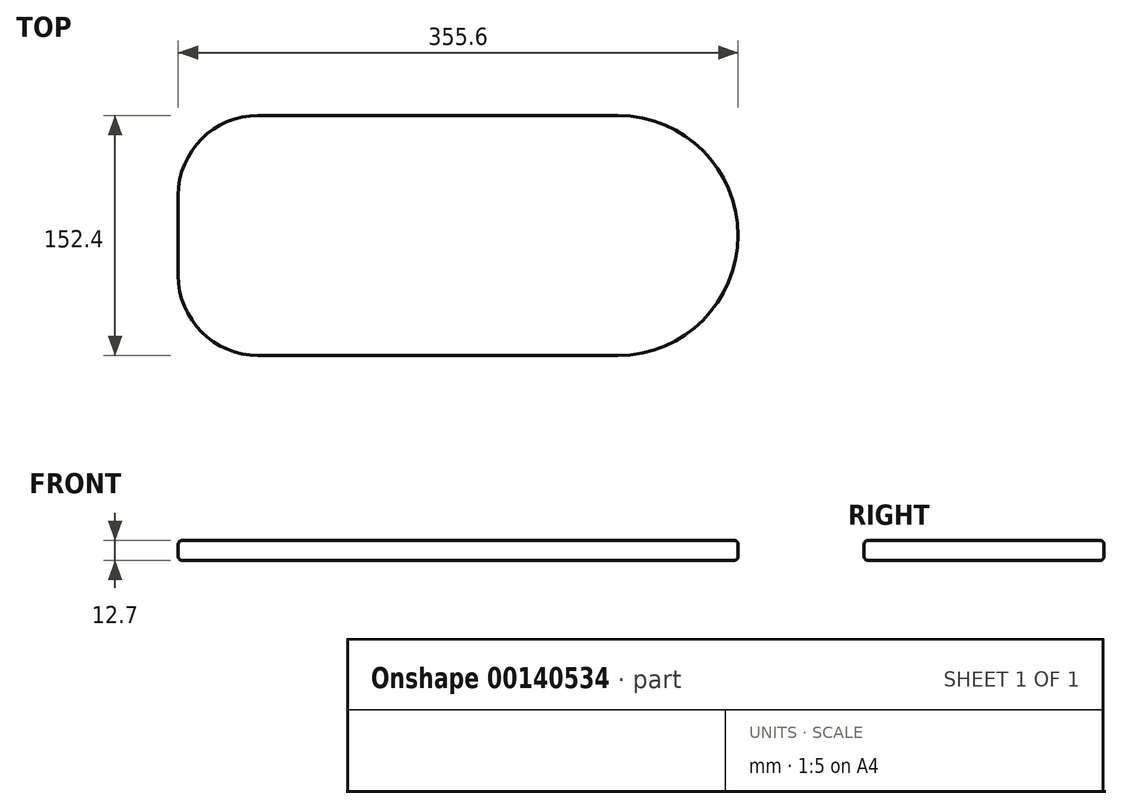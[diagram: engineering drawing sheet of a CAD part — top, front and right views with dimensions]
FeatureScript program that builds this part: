
annotation { "Feature Type Name" : "Feature", "Feature Type Description" : "" }
export const myFeature = defineFeature(function(context is Context, id is Id, definition is map)
    precondition{}
    {
        {
            var Q0;
            Q0=qCreatedBy(makeId("Top.planeOp"),FACE);
            var sketch = newSketch(context, id + "F0", { "sketchPlane" : qUnion([Q0])});
            skLineSegment(sketch, "E0.bottom", {"start": v(177.8, -76.2) * mm, "end": v(-177.8, -76.2) * mm});
            skLineSegment(sketch, "E0.top", {"start": v(177.8, 76.2) * mm, "end": v(-177.8, 76.2) * mm});
            skLineSegment(sketch, "E0.left", {"start": v(177.8, -76.2) * mm, "end": v(177.8, 76.2) * mm});
            skLineSegment(sketch, "E0.right", {"start": v(-177.8, -76.2) * mm, "end": v(-177.8, 76.2) * mm});
            skPoint(sketch, "E0.middle", {"position": v(0, 0) * mm});
            skSolve(sketch);
        }
        {
            var Q0;
            Q0=makeQuery(id+"F0.imprint","IMPRINT",FACE,{"disambiguationData":[TD([[makeQuery(id+"F0.imprint","IMPRINT",EDGE,{"derivedFrom":sQuery(id+"F0.wireOp",EDGE,"E0.bottom")}),-1.0]])]});
            extrude(context, id + "F1", {"entities" : qUnion([Q0]), "depth" : 12.7 * mm});
        }
        {
            var Q0;
            Q0=makeQuery(id+"F1.opExtrude","SWEPT_EDGE",EDGE,{"disambiguationData":[OSD([sQuery(id+"F0.wireOp",EDGE,"E0.top"),sQuery(id+"F0.wireOp",EDGE,"E0.left")])]});
            fillet(context, id + "F2", {"entities" : qUnion([Q0]), "radius" : 76.2 * mm, "tangentPropagation" : true, "allowEdgeOverflow" : false});
        }
        {
            var Q0;
            Q0=makeQuery(id+"F1.opExtrude","SWEPT_EDGE",EDGE,{"disambiguationData":[OSD([sQuery(id+"F0.wireOp",EDGE,"E0.bottom"),sQuery(id+"F0.wireOp",EDGE,"E0.left")])]});
            fillet(context, id + "F3", {"entities" : qUnion([Q0]), "radius" : 76.2 * mm, "tangentPropagation" : true, "allowEdgeOverflow" : false});
        }
        {
            var Q0;
            Q0=makeQuery(id+"F1.opExtrude","SWEPT_EDGE",EDGE,{"disambiguationData":[OSD([sQuery(id+"F0.wireOp",EDGE,"E0.top"),sQuery(id+"F0.wireOp",EDGE,"E0.right")])]});
            fillet(context, id + "F4", {"entities" : qUnion([Q0]), "radius" : 50.8 * mm, "tangentPropagation" : true, "allowEdgeOverflow" : false});
        }
        {
            var Q0;
            Q0=makeQuery(id+"F1.opExtrude","SWEPT_EDGE",EDGE,{"disambiguationData":[OSD([sQuery(id+"F0.wireOp",EDGE,"E0.bottom"),sQuery(id+"F0.wireOp",EDGE,"E0.right")])]});
            fillet(context, id + "F5", {"entities" : qUnion([Q0]), "radius" : 50.8 * mm, "tangentPropagation" : true, "allowEdgeOverflow" : false});
        }
        {
            var Q0;
            Q0=makeQuery(id+"F1.opExtrude","CAP_EDGE",EDGE,{"disambiguationData":[OSD([sQuery(id+"F0.wireOp",EDGE,"E0.top")])],"isStart":false});
            var Q1;
            Q1=makeQuery(id+"F1.opExtrude","CAP_EDGE",EDGE,{"disambiguationData":[OSD([sQuery(id+"F0.wireOp",EDGE,"E0.top")])],"isStart":true});
            fillet(context, id + "F6", {"entities" : qUnion([Q0, Q1]), "radius" : 2.54 * mm, "tangentPropagation" : true, "allowEdgeOverflow" : false});
        }
    });
